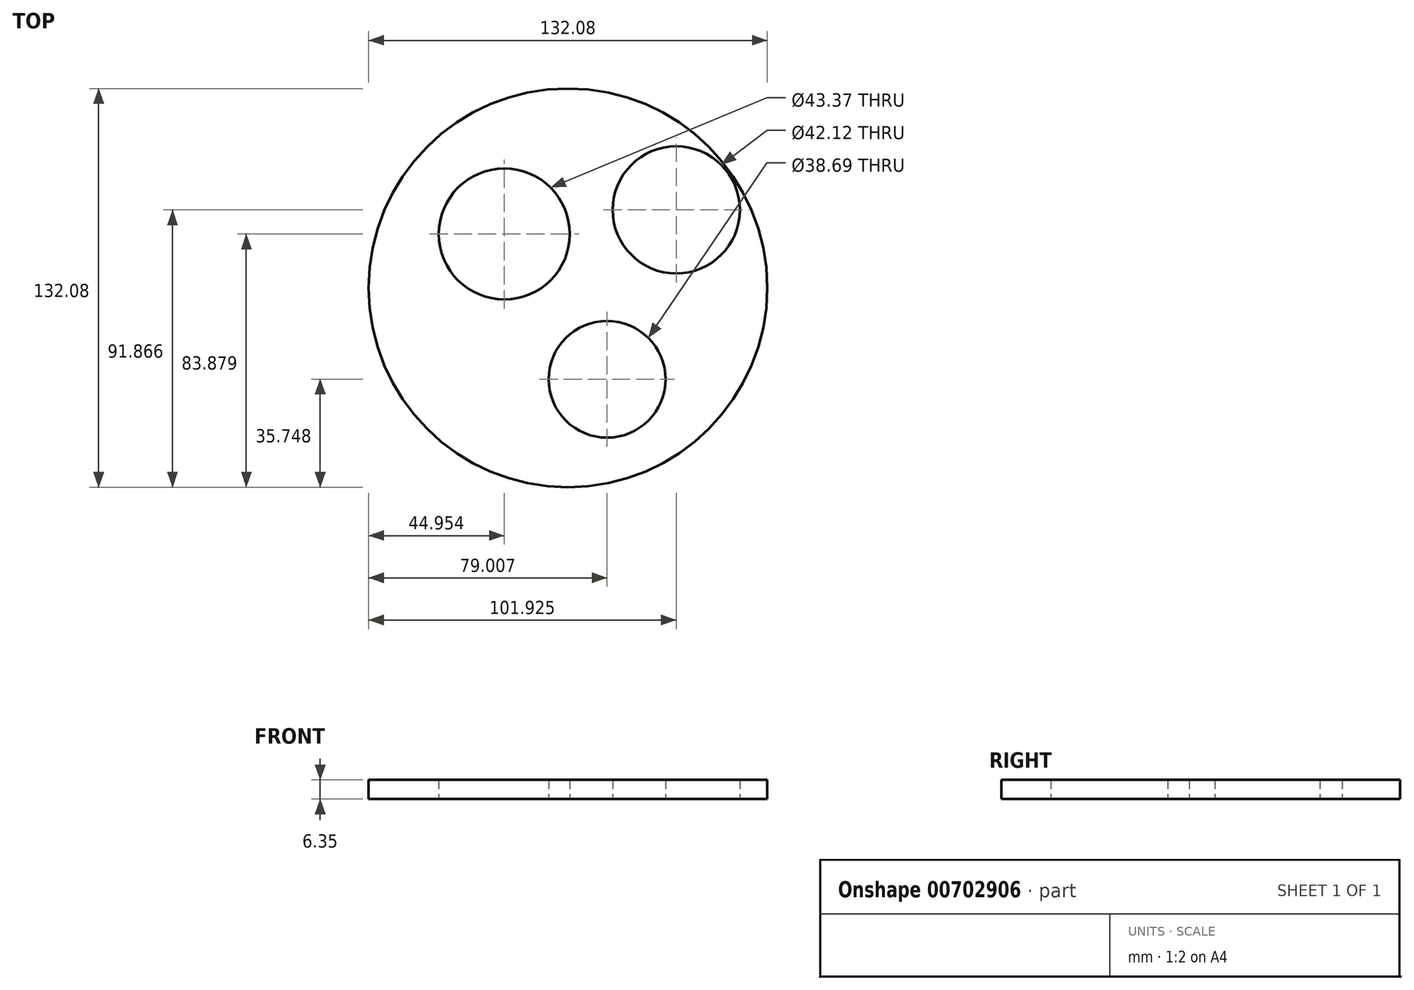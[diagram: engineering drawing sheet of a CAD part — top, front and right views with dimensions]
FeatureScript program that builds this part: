
annotation { "Feature Type Name" : "Feature", "Feature Type Description" : "" }
export const myFeature = defineFeature(function(context is Context, id is Id, definition is map)
    precondition{}
    {
        {
            var Q0;
            Q0=qCreatedBy(makeId("Top.planeOp"),FACE);
            var sketch = newSketch(context, id + "F0", { "sketchPlane" : qUnion([Q0])});
            skCircle(sketch, "E0", {"center": v(0, 0) * mm, "radius": 66.04 * mm});
            skSolve(sketch);
        }
        {
            var Q0;
            Q0 = qSketchRegion(id + "F0", true);
            extrude(context, id + "F1", {"entities" : qUnion([Q0]), "depth" : 6.35 * mm, "offsetDistance" : 25.4 * mm});
        }
        {
            var Q0;
            Q0=qCreatedBy(makeId("Top.planeOp"),FACE);
            var sketch = newSketch(context, id + "F2", { "sketchPlane" : qUnion([Q0])});
            skCircle(sketch, "E1", {"center": v(-21.09, 17.84) * mm, "radius": 21.68 * mm});
            skCircle(sketch, "E2", {"center": v(35.89, 25.83) * mm, "radius": 21.06 * mm});
            skCircle(sketch, "E3", {"center": v(12.97, -30.3) * mm, "radius": 19.34 * mm});
            skSolve(sketch);
        }
        {
            var Q0;
            Q0 = qSketchRegion(id + "F2", true);
            extrude(context, id + "F3", {"entities" : qUnion([Q0]), "operationType" : NewBodyOperationType.REMOVE, "endBound" : BoundingType.THROUGH_ALL, "depth" : 6.35 * mm, "offsetDistance" : 25.4 * mm});
        }
    });
